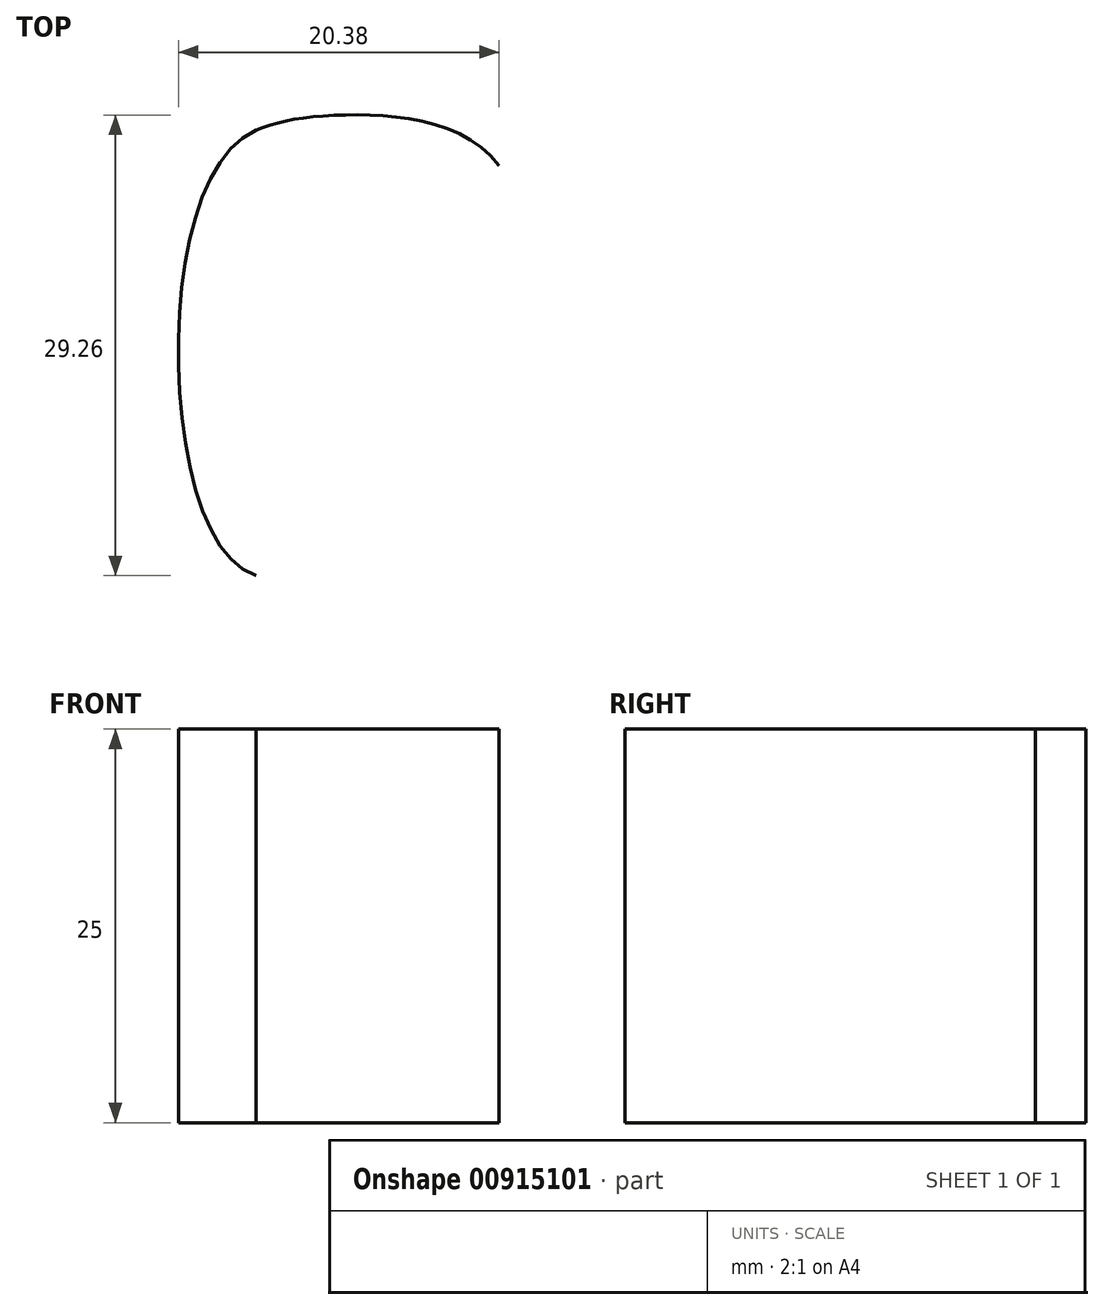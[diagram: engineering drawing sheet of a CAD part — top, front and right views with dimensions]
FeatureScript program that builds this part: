
annotation { "Feature Type Name" : "Feature", "Feature Type Description" : "" }
export const myFeature = defineFeature(function(context is Context, id is Id, definition is map)
    precondition{}
    {
        {
            var Q0;
            Q0=qCreatedBy(makeId("Top.planeOp"),FACE);
            var sketch = newSketch(context, id + "F0", { "sketchPlane" : qUnion([Q0])});
            skLineSegment(sketch, "E0.bottom", {"start": v(10, -15) * mm, "end": v(-10, -15) * mm, "construction": true});
            skLineSegment(sketch, "E0.top", {"start": v(10, 15) * mm, "end": v(-10, 15) * mm, "construction": true});
            skLineSegment(sketch, "E0.left", {"start": v(10, -15) * mm, "end": v(10, 15) * mm, "construction": true});
            skLineSegment(sketch, "E0.right", {"start": v(-10, -15) * mm, "end": v(-10, 15) * mm, "construction": true});
            skPoint(sketch, "E0.middle", {"position": v(0, 0) * mm});
            skPoint(sketch, "E1", {"position": v(-10, 0) * mm});
            skFitSpline(sketch, "E2", {"points": [v(-5.45, 14.04) * mm, v(0, 15) * mm, v(10, 11.8) * mm], "startDerivative": vector(9.57, 4.18) * mm, "endDerivative": vector(11.62, -15.25) * mm});
            skFitSpline(sketch, "E3", {"points": [v(-5.45, 14.04) * mm, v(-10.38, 0) * mm, v(-5.45, -14.25) * mm], "startDerivative": vector(-20.45, -8.94) * mm, "endDerivative": vector(20.17, -6.6) * mm});
            skSolve(sketch);
        }
        {
            var Q0;
            Q0 = qSketchRegion(id + "F0", true);
            var Q1;
            Q1=sQuery(id+"F0.wireOp",EDGE,"E3");
            var Q2;
            Q2=sQuery(id+"F0.wireOp",EDGE,"E2");
            extrude(context, id + "F1", {"entities" : qUnion([Q0]), "bodyType" : ToolBodyType.SURFACE, "surfaceEntities" : qUnion([Q1, Q2]), "depth" : 25 * mm, "offsetDistance" : 25 * mm});
        }
    });
